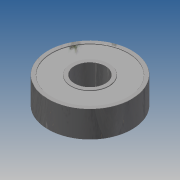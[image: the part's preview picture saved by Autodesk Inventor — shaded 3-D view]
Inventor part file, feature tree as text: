
AUTODESK INVENTOR PART (.ipt)
format: ipt  version: 2015 SP1 (Build 190203100, 203)  size: 151,552 bytes
history: native  units: mm
features: chamfer x8, extrude x2, sketch x2, mirror x1, projected_geometry x1
ambient origin geometry x8: Origin, YZ Plane, XZ Plane, XY Plane, X Axis, Y Axis, Z Axis, Center Point
bodies: Volumenkörper1 (feature_tree)
feature tree (14):
  extrude  "Extrusion1"  Depth=8.0mm
  extrude  "Extrusion2"  Depth=10.0mm
  mirror  "Spiegeln1"
  chamfer  "Fase1"  Distance=20.0mm
  chamfer  "Fase2"  Distance=0.2mm
  chamfer  "Fase3"  Distance=0.05mm Angle=45.0deg
  chamfer  "Fase4"  Distance=0.05mm Angle=45.0deg
  chamfer  "Fase5"  Distance=0.05mm Angle=45.0deg
  chamfer  "Fase6"  Distance=0.05mm Angle=45.0deg
  chamfer  "Fase7"  Distance=0.05mm Angle=45.0deg
  chamfer  "Fase8"  Distance=0.05mm Angle=45.0deg
  sketch  "Skizze1"  dims[d0=22.0mm d1=8.0mm]
  sketch  "Skizze2"  dims[d2=7.0mm d3=0.0mm d4=10.0mm d5=20.0mm d6=0.2mm d7=0.0mm d8=0.05mm d9=2.0mm d10=45.0deg d11=0.05mm d12=2.0mm d13=45.0deg d14=0.05mm d15=2.0mm d16=45.0deg d17=0.05mm d18=2.0mm d19=45.0deg d20=0.05mm d21=2.0mm d22=45.0deg d23=0.05mm d24=2.0mm d25=45.0deg d26=0.05mm d27=2.0mm d28=45.0deg d29=0.05mm d30=2.0mm d31=45.0deg]
  projected_geometry  "Projizierte Kontur1"
